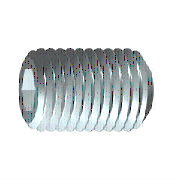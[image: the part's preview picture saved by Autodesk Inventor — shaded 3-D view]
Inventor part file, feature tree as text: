
AUTODESK INVENTOR PART (.ipt)
format: ipt  version: 2013 (Build 170138000, 138)  size: 173,056 bytes
history: native  units: mm (DEFAULTED — no unit token found)
features: sketch x2, extrude x1, other x1, plane x1
ambient origin geometry x8: Origin, YZ Plane, XZ Plane, XY Plane, X Axis, Y Axis, Z Axis, Center Point
bodies: Solid1 (feature_tree), Body (feature_tree)
feature tree (5):
  extrude  "Slot"  TaperAngle=60.0deg  [1 undecoded]
  other  "Work Axis1"
  plane  "Work Plane1"
  sketch  "Sketch1"  dims[d0=2.032mm d1=60.0deg]
  sketch  "Sketch2"  dims[d2=4.1656mm d3=2.287693mm d6=90.0deg d4=4.7625mm d5=10.297443mm d7=2.0828mm d8=2.032mm d9=0.0mm d10=1.0414mm d11=45.0deg d12=0.42926mm d13=45.0deg d14=4.7625mm d15=0.0mm d16=0.0mm d33=1.0414mm d34=0.42926mm d35=0.0mm d37=0.0mm]
note: 1 required parameter value undecoded (feature->parameter linkage not recoverable at this tier; creation-order binding heuristic only, values carry confidence <= 0.55)
